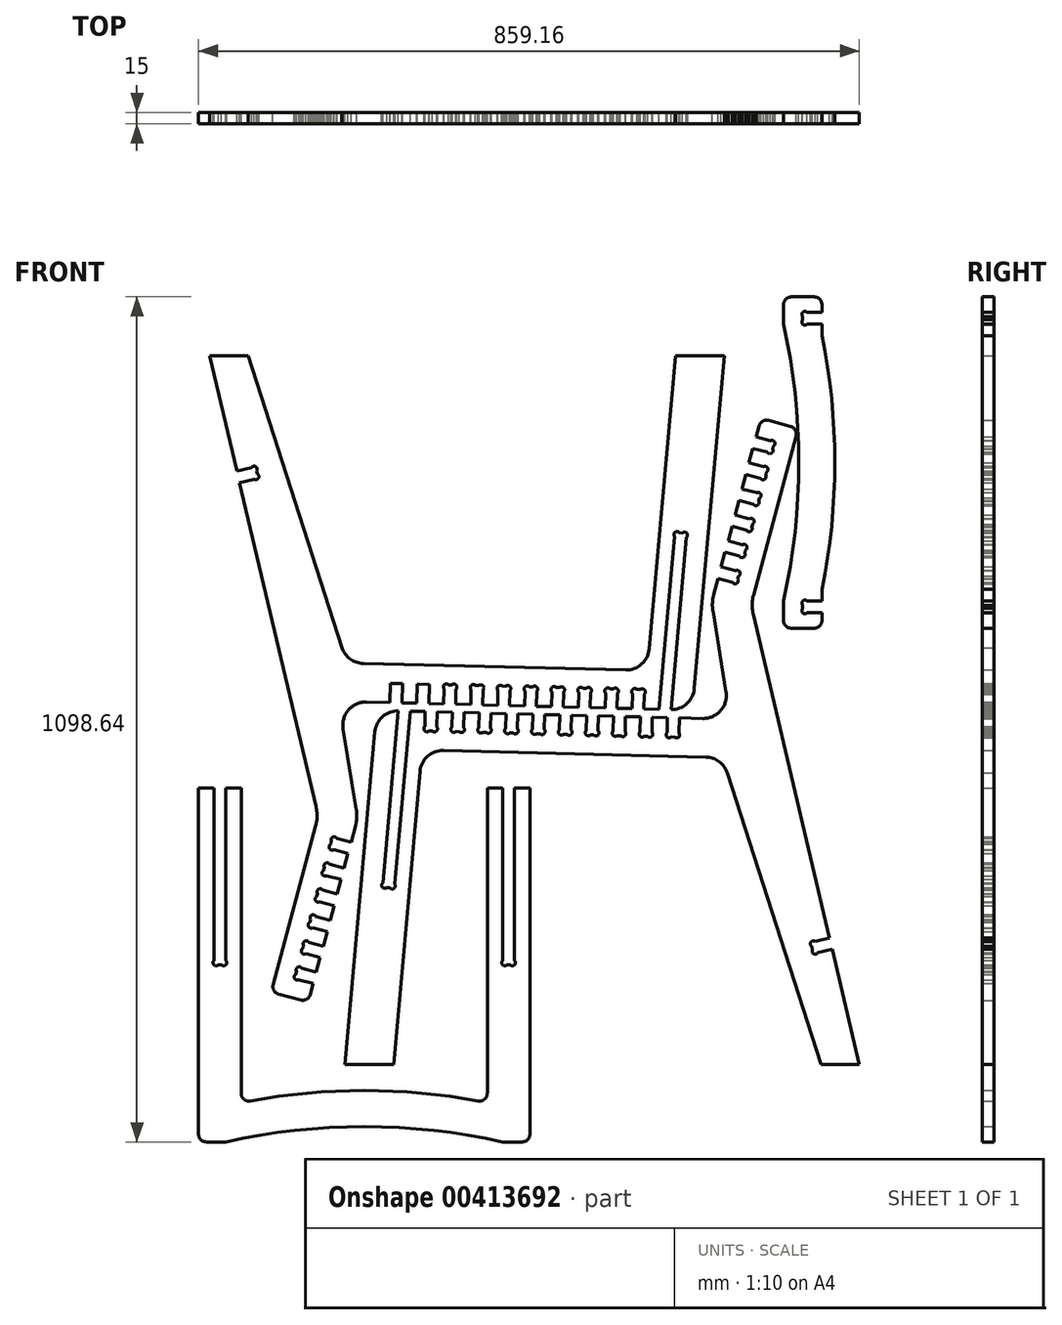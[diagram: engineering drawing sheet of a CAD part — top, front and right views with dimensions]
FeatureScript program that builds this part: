
annotation { "Feature Type Name" : "Feature", "Feature Type Description" : "" }
export const myFeature = defineFeature(function(context is Context, id is Id, definition is map)
    precondition{}
    {
        {
            var Q0;
            Q0=qCreatedBy(makeId("Front.planeOp"),FACE);
            var sketch = newSketch(context, id + "F0", { "sketchPlane" : qUnion([Q0])});
            skLineSegment(sketch, "E0", {"start": v(-375.2, 497.25) * mm, "end": v(-425.2, 497.25) * mm});
            skLineSegment(sketch, "E1", {"start": v(-425.2, 497.25) * mm, "end": v(-389.9, 347.46) * mm});
            skLineSegment(sketch, "E2", {"start": v(-389.9, 347.46) * mm, "end": v(-371.08, 351.9) * mm});
            skArc(sketch, "E3", {"start": v(-371.08, 351.9) * mm, "mid": v(-365.57, 353.2) * mm, "end": v(-364.28, 347.69) * mm});
            skLineSegment(sketch, "E4", {"start": v(-364.28, 347.69) * mm, "end": v(-363.34, 343.71) * mm});
            skArc(sketch, "E5", {"start": v(-363.34, 343.71) * mm, "mid": v(-362.04, 338.2) * mm, "end": v(-367.55, 336.91) * mm});
            skLineSegment(sketch, "E6", {"start": v(-367.55, 336.91) * mm, "end": v(-386.37, 332.48) * mm});
            skLineSegment(sketch, "E7", {"start": v(-386.37, 332.48) * mm, "end": v(-287.1, -88.96) * mm});
            skArc(sketch, "E8", {"start": v(-287.1, -88.96) * mm, "mid": v(-285.77, -101.18) * mm, "end": v(-287.47, -113.36) * mm});
            skLineSegment(sketch, "E9", {"start": v(-287.47, -113.36) * mm, "end": v(-342.89, -320.18) * mm});
            skArc(sketch, "E10", {"start": v(-342.89, -320.18) * mm, "mid": v(-341.89, -327.77) * mm, "end": v(-335.82, -332.42) * mm});
            skLineSegment(sketch, "E11", {"start": v(-335.82, -332.42) * mm, "end": v(-306.84, -340.19) * mm});
            skArc(sketch, "E12", {"start": v(-306.84, -340.19) * mm, "mid": v(-299.25, -339.19) * mm, "end": v(-294.6, -333.12) * mm});
            skLineSegment(sketch, "E13", {"start": v(-294.6, -333.12) * mm, "end": v(-290.77, -318.82) * mm});
            skLineSegment(sketch, "E14", {"start": v(-290.77, -318.82) * mm, "end": v(-309.45, -313.82) * mm});
            skArc(sketch, "E15", {"start": v(-309.45, -313.82) * mm, "mid": v(-314.91, -312.35) * mm, "end": v(-313.45, -306.9) * mm});
            skLineSegment(sketch, "E16", {"start": v(-313.45, -306.9) * mm, "end": v(-312.39, -302.94) * mm});
            skArc(sketch, "E17", {"start": v(-312.39, -302.94) * mm, "mid": v(-310.93, -297.48) * mm, "end": v(-305.46, -298.95) * mm});
            skLineSegment(sketch, "E18", {"start": v(-305.46, -298.95) * mm, "end": v(-286.78, -303.95) * mm});
            skLineSegment(sketch, "E19", {"start": v(-286.78, -303.95) * mm, "end": v(-281.7, -285.02) * mm});
            skLineSegment(sketch, "E20", {"start": v(-281.7, -285.02) * mm, "end": v(-300.39, -280.02) * mm});
            skArc(sketch, "E21", {"start": v(-300.39, -280.02) * mm, "mid": v(-305.85, -278.55) * mm, "end": v(-304.39, -273.09) * mm});
            skLineSegment(sketch, "E22", {"start": v(-304.39, -273.09) * mm, "end": v(-303.33, -269.14) * mm});
            skArc(sketch, "E23", {"start": v(-303.33, -269.14) * mm, "mid": v(-301.87, -263.68) * mm, "end": v(-296.4, -265.14) * mm});
            skLineSegment(sketch, "E24", {"start": v(-296.4, -265.14) * mm, "end": v(-277.72, -270.15) * mm});
            skLineSegment(sketch, "E25", {"start": v(-277.72, -270.15) * mm, "end": v(-272.65, -251.22) * mm});
            skLineSegment(sketch, "E26", {"start": v(-272.65, -251.22) * mm, "end": v(-291.33, -246.21) * mm});
            skArc(sketch, "E27", {"start": v(-291.33, -246.21) * mm, "mid": v(-296.8, -244.75) * mm, "end": v(-295.33, -239.29) * mm});
            skLineSegment(sketch, "E28", {"start": v(-295.33, -239.29) * mm, "end": v(-294.27, -235.34) * mm});
            skArc(sketch, "E29", {"start": v(-294.27, -235.34) * mm, "mid": v(-292.81, -229.88) * mm, "end": v(-287.35, -231.34) * mm});
            skLineSegment(sketch, "E30", {"start": v(-287.35, -231.34) * mm, "end": v(-268.66, -236.34) * mm});
            skLineSegment(sketch, "E31", {"start": v(-268.66, -236.34) * mm, "end": v(-263.6, -217.42) * mm});
            skLineSegment(sketch, "E32", {"start": v(-263.6, -217.42) * mm, "end": v(-282.27, -212.4) * mm});
            skArc(sketch, "E33", {"start": v(-282.27, -212.4) * mm, "mid": v(-287.74, -210.95) * mm, "end": v(-286.27, -205.48) * mm});
            skLineSegment(sketch, "E34", {"start": v(-286.27, -205.48) * mm, "end": v(-285.22, -201.54) * mm});
            skArc(sketch, "E35", {"start": v(-285.22, -201.54) * mm, "mid": v(-283.75, -196.07) * mm, "end": v(-278.29, -197.54) * mm});
            skLineSegment(sketch, "E36", {"start": v(-278.29, -197.54) * mm, "end": v(-259.6, -202.54) * mm});
            skLineSegment(sketch, "E37", {"start": v(-259.6, -202.54) * mm, "end": v(-254.54, -183.61) * mm});
            skLineSegment(sketch, "E38", {"start": v(-254.54, -183.61) * mm, "end": v(-273.22, -178.6) * mm});
            skArc(sketch, "E39", {"start": v(-273.22, -178.6) * mm, "mid": v(-278.68, -177.14) * mm, "end": v(-277.22, -171.68) * mm});
            skLineSegment(sketch, "E40", {"start": v(-277.22, -171.68) * mm, "end": v(-276.16, -167.73) * mm});
            skArc(sketch, "E41", {"start": v(-276.16, -167.73) * mm, "mid": v(-274.7, -162.27) * mm, "end": v(-269.23, -163.73) * mm});
            skLineSegment(sketch, "E42", {"start": v(-269.23, -163.73) * mm, "end": v(-250.55, -168.74) * mm});
            skLineSegment(sketch, "E43", {"start": v(-250.55, -168.74) * mm, "end": v(-245.48, -149.8) * mm});
            skLineSegment(sketch, "E44", {"start": v(-245.48, -149.8) * mm, "end": v(-264.16, -144.8) * mm});
            skArc(sketch, "E45", {"start": v(-264.16, -144.8) * mm, "mid": v(-269.62, -143.34) * mm, "end": v(-268.16, -137.88) * mm});
            skLineSegment(sketch, "E46", {"start": v(-268.16, -137.88) * mm, "end": v(-267.1, -133.93) * mm});
            skArc(sketch, "E47", {"start": v(-267.1, -133.93) * mm, "mid": v(-265.64, -128.47) * mm, "end": v(-260.17, -129.93) * mm});
            skLineSegment(sketch, "E48", {"start": v(-260.17, -129.93) * mm, "end": v(-241.5, -134.94) * mm});
            skLineSegment(sketch, "E49", {"start": v(-241.5, -134.94) * mm, "end": v(-235.8, -113.7) * mm});
            skArc(sketch, "E50", {"start": v(-235.8, -113.7) * mm, "mid": v(-234.15, -103.12) * mm, "end": v(-234.8, -92.43) * mm});
            skLineSegment(sketch, "E51", {"start": v(-234.8, -92.43) * mm, "end": v(-251.88, 12.44) * mm});
            skArc(sketch, "E52", {"start": v(-251.88, 12.44) * mm, "mid": v(-244.88, 36.98) * mm, "end": v(-221.53, 47.25) * mm});
            skLineSegment(sketch, "E53", {"start": v(-221.53, 47.25) * mm, "end": v(-190.95, 46.49) * mm});
            skLineSegment(sketch, "E54", {"start": v(-190.95, 46.49) * mm, "end": v(-190.33, 71.48) * mm});
            skLineSegment(sketch, "E55", {"start": v(-190.33, 71.48) * mm, "end": v(-174.93, 71.1) * mm});
            skLineSegment(sketch, "E56", {"start": v(-174.93, 71.1) * mm, "end": v(-175.56, 46.1) * mm});
            skLineSegment(sketch, "E57", {"start": v(-175.56, 46.1) * mm, "end": v(-155.97, 45.62) * mm});
            skLineSegment(sketch, "E58", {"start": v(-155.97, 45.62) * mm, "end": v(-155.34, 70.6) * mm});
            skLineSegment(sketch, "E59", {"start": v(-155.34, 70.6) * mm, "end": v(-139.95, 70.22) * mm});
            skLineSegment(sketch, "E60", {"start": v(-139.95, 70.22) * mm, "end": v(-140.57, 45.23) * mm});
            skLineSegment(sketch, "E61", {"start": v(-140.57, 45.23) * mm, "end": v(-120.98, 44.74) * mm});
            skLineSegment(sketch, "E62", {"start": v(-120.98, 44.74) * mm, "end": v(-120.5, 64.08) * mm});
            skArc(sketch, "E63", {"start": v(-120.5, 64.08) * mm, "mid": v(-120.36, 69.73) * mm, "end": v(-114.7, 69.6) * mm});
            skLineSegment(sketch, "E64", {"start": v(-114.7, 69.6) * mm, "end": v(-110.62, 69.5) * mm});
            skArc(sketch, "E65", {"start": v(-110.62, 69.5) * mm, "mid": v(-104.97, 69.35) * mm, "end": v(-105.1, 63.7) * mm});
            skLineSegment(sketch, "E66", {"start": v(-105.1, 63.7) * mm, "end": v(-105.59, 44.36) * mm});
            skLineSegment(sketch, "E67", {"start": v(-105.59, 44.36) * mm, "end": v(-86, 43.87) * mm});
            skLineSegment(sketch, "E68", {"start": v(-86, 43.87) * mm, "end": v(-85.51, 63.2) * mm});
            skArc(sketch, "E69", {"start": v(-85.51, 63.2) * mm, "mid": v(-85.37, 68.86) * mm, "end": v(-79.72, 68.72) * mm});
            skLineSegment(sketch, "E70", {"start": v(-79.72, 68.72) * mm, "end": v(-75.64, 68.62) * mm});
            skArc(sketch, "E71", {"start": v(-75.64, 68.62) * mm, "mid": v(-69.98, 68.48) * mm, "end": v(-70.12, 62.82) * mm});
            skLineSegment(sketch, "E72", {"start": v(-70.12, 62.82) * mm, "end": v(-70.6, 43.49) * mm});
            skLineSegment(sketch, "E73", {"start": v(-70.6, 43.49) * mm, "end": v(-51.01, 43) * mm});
            skLineSegment(sketch, "E74", {"start": v(-51.01, 43) * mm, "end": v(-50.53, 62.33) * mm});
            skArc(sketch, "E75", {"start": v(-50.53, 62.33) * mm, "mid": v(-50.39, 67.99) * mm, "end": v(-44.73, 67.85) * mm});
            skLineSegment(sketch, "E76", {"start": v(-44.73, 67.85) * mm, "end": v(-40.65, 67.75) * mm});
            skArc(sketch, "E77", {"start": v(-40.65, 67.75) * mm, "mid": v(-35, 67.6) * mm, "end": v(-35.14, 61.95) * mm});
            skLineSegment(sketch, "E78", {"start": v(-35.14, 61.95) * mm, "end": v(-35.62, 42.62) * mm});
            skLineSegment(sketch, "E79", {"start": v(-35.62, 42.62) * mm, "end": v(-16.03, 42.13) * mm});
            skLineSegment(sketch, "E80", {"start": v(-16.03, 42.13) * mm, "end": v(-15.55, 61.46) * mm});
            skArc(sketch, "E81", {"start": v(-15.55, 61.46) * mm, "mid": v(-15.4, 67.12) * mm, "end": v(-9.75, 66.98) * mm});
            skLineSegment(sketch, "E82", {"start": v(-9.75, 66.98) * mm, "end": v(-5.67, 66.87) * mm});
            skArc(sketch, "E83", {"start": v(-5.67, 66.87) * mm, "mid": v(-0.01, 66.73) * mm, "end": v(-0.15, 61.08) * mm});
            skLineSegment(sketch, "E84", {"start": v(-0.15, 61.08) * mm, "end": v(-0.63, 41.74) * mm});
            skLineSegment(sketch, "E85", {"start": v(-0.63, 41.74) * mm, "end": v(18.96, 41.26) * mm});
            skLineSegment(sketch, "E86", {"start": v(18.96, 41.26) * mm, "end": v(19.44, 60.6) * mm});
            skArc(sketch, "E87", {"start": v(19.44, 60.6) * mm, "mid": v(19.58, 66.24) * mm, "end": v(25.23, 66.1) * mm});
            skLineSegment(sketch, "E88", {"start": v(25.23, 66.1) * mm, "end": v(29.32, 66) * mm});
            skArc(sketch, "E89", {"start": v(29.32, 66) * mm, "mid": v(34.97, 65.86) * mm, "end": v(34.83, 60.2) * mm});
            skLineSegment(sketch, "E90", {"start": v(34.83, 60.2) * mm, "end": v(34.35, 40.87) * mm});
            skLineSegment(sketch, "E91", {"start": v(34.35, 40.87) * mm, "end": v(53.94, 40.38) * mm});
            skLineSegment(sketch, "E92", {"start": v(53.94, 40.38) * mm, "end": v(54.42, 59.72) * mm});
            skArc(sketch, "E93", {"start": v(54.42, 59.72) * mm, "mid": v(54.56, 65.37) * mm, "end": v(60.22, 65.23) * mm});
            skLineSegment(sketch, "E94", {"start": v(60.22, 65.23) * mm, "end": v(64.3, 65.13) * mm});
            skArc(sketch, "E95", {"start": v(64.3, 65.13) * mm, "mid": v(69.96, 64.99) * mm, "end": v(69.82, 59.33) * mm});
            skLineSegment(sketch, "E96", {"start": v(69.82, 59.33) * mm, "end": v(69.34, 40) * mm});
            skLineSegment(sketch, "E97", {"start": v(69.34, 40) * mm, "end": v(88.93, 39.51) * mm});
            skLineSegment(sketch, "E98", {"start": v(88.93, 39.51) * mm, "end": v(89.4, 58.85) * mm});
            skArc(sketch, "E99", {"start": v(89.4, 58.85) * mm, "mid": v(89.55, 64.5) * mm, "end": v(95.2, 64.36) * mm});
            skLineSegment(sketch, "E100", {"start": v(95.2, 64.36) * mm, "end": v(99.29, 64.26) * mm});
            skArc(sketch, "E101", {"start": v(99.29, 64.26) * mm, "mid": v(104.94, 64.12) * mm, "end": v(104.8, 58.46) * mm});
            skLineSegment(sketch, "E102", {"start": v(104.8, 58.46) * mm, "end": v(104.32, 39.13) * mm});
            skLineSegment(sketch, "E103", {"start": v(104.32, 39.13) * mm, "end": v(123.91, 38.64) * mm});
            skLineSegment(sketch, "E104", {"start": v(123.91, 38.64) * mm, "end": v(124.4, 57.97) * mm});
            skArc(sketch, "E105", {"start": v(124.4, 57.97) * mm, "mid": v(124.53, 63.63) * mm, "end": v(130.19, 63.49) * mm});
            skLineSegment(sketch, "E106", {"start": v(130.19, 63.49) * mm, "end": v(134.27, 63.39) * mm});
            skArc(sketch, "E107", {"start": v(134.27, 63.39) * mm, "mid": v(139.93, 63.24) * mm, "end": v(139.79, 57.6) * mm});
            skLineSegment(sketch, "E108", {"start": v(139.79, 57.6) * mm, "end": v(139.3, 38.26) * mm});
            skLineSegment(sketch, "E109", {"start": v(139.3, 38.26) * mm, "end": v(158.88, 37.77) * mm});
            skLineSegment(sketch, "E110", {"start": v(158.88, 37.77) * mm, "end": v(179.13, 262.38) * mm});
            skArc(sketch, "E111", {"start": v(179.13, 262.38) * mm, "mid": v(179.64, 268.01) * mm, "end": v(185.27, 267.5) * mm});
            skLineSegment(sketch, "E112", {"start": v(185.27, 267.5) * mm, "end": v(189.34, 267.14) * mm});
            skArc(sketch, "E113", {"start": v(189.34, 267.14) * mm, "mid": v(194.97, 266.63) * mm, "end": v(194.46, 261) * mm});
            skLineSegment(sketch, "E114", {"start": v(194.46, 261) * mm, "end": v(174.3, 37.38) * mm});
            skArc(sketch, "E115", {"start": v(174.3, 37.38) * mm, "mid": v(194.88, 45.05) * mm, "end": v(204.71, 64.68) * mm});
            skLineSegment(sketch, "E116", {"start": v(204.71, 64.68) * mm, "end": v(243.7, 497.25) * mm});
            skLineSegment(sketch, "E117", {"start": v(243.7, 497.25) * mm, "end": v(180.44, 497.25) * mm});
            skLineSegment(sketch, "E118", {"start": v(180.44, 497.25) * mm, "end": v(146.08, 116.15) * mm});
            skArc(sketch, "E119", {"start": v(146.08, 116.15) * mm, "mid": v(136.17, 96.45) * mm, "end": v(115.46, 88.86) * mm});
            skLineSegment(sketch, "E120", {"start": v(115.46, 88.86) * mm, "end": v(-225.61, 97.36) * mm});
            skArc(sketch, "E121", {"start": v(-225.61, 97.36) * mm, "mid": v(-242.67, 103.21) * mm, "end": v(-253.3, 117.79) * mm});
            skLineSegment(sketch, "E122", {"start": v(-253.3, 117.79) * mm, "end": v(-375.2, 497.25) * mm});
            skLineSegment(sketch, "E123", {"start": v(369.36, -424.14) * mm, "end": v(419.36, -424.14) * mm});
            skLineSegment(sketch, "E124", {"start": v(419.36, -424.14) * mm, "end": v(384.07, -274.36) * mm});
            skLineSegment(sketch, "E125", {"start": v(384.07, -274.36) * mm, "end": v(365.25, -278.8) * mm});
            skArc(sketch, "E126", {"start": v(365.25, -278.8) * mm, "mid": v(359.74, -280.09) * mm, "end": v(358.44, -274.58) * mm});
            skLineSegment(sketch, "E127", {"start": v(358.44, -274.58) * mm, "end": v(357.5, -270.6) * mm});
            skArc(sketch, "E128", {"start": v(357.5, -270.6) * mm, "mid": v(356.21, -265.1) * mm, "end": v(361.72, -263.8) * mm});
            skLineSegment(sketch, "E129", {"start": v(361.72, -263.8) * mm, "end": v(380.54, -259.37) * mm});
            skLineSegment(sketch, "E130", {"start": v(380.54, -259.37) * mm, "end": v(281.26, 162.06) * mm});
            skArc(sketch, "E131", {"start": v(281.26, 162.06) * mm, "mid": v(279.94, 174.29) * mm, "end": v(281.64, 186.46) * mm});
            skLineSegment(sketch, "E132", {"start": v(281.64, 186.46) * mm, "end": v(337.05, 393.28) * mm});
            skArc(sketch, "E133", {"start": v(337.05, 393.28) * mm, "mid": v(336.05, 400.87) * mm, "end": v(329.98, 405.53) * mm});
            skLineSegment(sketch, "E134", {"start": v(329.98, 405.53) * mm, "end": v(301, 413.3) * mm});
            skArc(sketch, "E135", {"start": v(301, 413.3) * mm, "mid": v(293.42, 412.3) * mm, "end": v(288.76, 406.22) * mm});
            skLineSegment(sketch, "E136", {"start": v(288.76, 406.22) * mm, "end": v(284.93, 391.93) * mm});
            skLineSegment(sketch, "E137", {"start": v(284.93, 391.93) * mm, "end": v(303.61, 386.92) * mm});
            skArc(sketch, "E138", {"start": v(303.61, 386.92) * mm, "mid": v(309.08, 385.46) * mm, "end": v(307.61, 380) * mm});
            skLineSegment(sketch, "E139", {"start": v(307.61, 380) * mm, "end": v(306.56, 376.05) * mm});
            skArc(sketch, "E140", {"start": v(306.56, 376.05) * mm, "mid": v(305.1, 370.59) * mm, "end": v(299.63, 372.05) * mm});
            skLineSegment(sketch, "E141", {"start": v(299.63, 372.05) * mm, "end": v(280.95, 377.06) * mm});
            skLineSegment(sketch, "E142", {"start": v(280.95, 377.06) * mm, "end": v(275.87, 358.13) * mm});
            skLineSegment(sketch, "E143", {"start": v(275.87, 358.13) * mm, "end": v(294.56, 353.12) * mm});
            skArc(sketch, "E144", {"start": v(294.56, 353.12) * mm, "mid": v(300.02, 351.66) * mm, "end": v(298.56, 346.2) * mm});
            skLineSegment(sketch, "E145", {"start": v(298.56, 346.2) * mm, "end": v(297.5, 342.25) * mm});
            skArc(sketch, "E146", {"start": v(297.5, 342.25) * mm, "mid": v(296.03, 336.78) * mm, "end": v(290.57, 338.25) * mm});
            skLineSegment(sketch, "E147", {"start": v(290.57, 338.25) * mm, "end": v(271.89, 343.25) * mm});
            skLineSegment(sketch, "E148", {"start": v(271.89, 343.25) * mm, "end": v(266.82, 324.32) * mm});
            skLineSegment(sketch, "E149", {"start": v(266.82, 324.32) * mm, "end": v(285.5, 319.32) * mm});
            skArc(sketch, "E150", {"start": v(285.5, 319.32) * mm, "mid": v(290.96, 317.85) * mm, "end": v(289.5, 312.4) * mm});
            skLineSegment(sketch, "E151", {"start": v(289.5, 312.4) * mm, "end": v(288.44, 308.44) * mm});
            skArc(sketch, "E152", {"start": v(288.44, 308.44) * mm, "mid": v(286.98, 302.98) * mm, "end": v(281.51, 304.44) * mm});
            skLineSegment(sketch, "E153", {"start": v(281.51, 304.44) * mm, "end": v(262.83, 309.45) * mm});
            skLineSegment(sketch, "E154", {"start": v(262.83, 309.45) * mm, "end": v(257.76, 290.52) * mm});
            skLineSegment(sketch, "E155", {"start": v(257.76, 290.52) * mm, "end": v(276.44, 285.51) * mm});
            skArc(sketch, "E156", {"start": v(276.44, 285.51) * mm, "mid": v(281.9, 284.05) * mm, "end": v(280.44, 278.59) * mm});
            skLineSegment(sketch, "E157", {"start": v(280.44, 278.59) * mm, "end": v(279.38, 274.64) * mm});
            skArc(sketch, "E158", {"start": v(279.38, 274.64) * mm, "mid": v(277.92, 269.18) * mm, "end": v(272.46, 270.64) * mm});
            skLineSegment(sketch, "E159", {"start": v(272.46, 270.64) * mm, "end": v(253.77, 275.65) * mm});
            skLineSegment(sketch, "E160", {"start": v(253.77, 275.65) * mm, "end": v(248.7, 256.72) * mm});
            skLineSegment(sketch, "E161", {"start": v(248.7, 256.72) * mm, "end": v(267.38, 251.71) * mm});
            skArc(sketch, "E162", {"start": v(267.38, 251.71) * mm, "mid": v(272.85, 250.25) * mm, "end": v(271.38, 244.78) * mm});
            skLineSegment(sketch, "E163", {"start": v(271.38, 244.78) * mm, "end": v(270.33, 240.84) * mm});
            skArc(sketch, "E164", {"start": v(270.33, 240.84) * mm, "mid": v(268.86, 235.37) * mm, "end": v(263.4, 236.84) * mm});
            skLineSegment(sketch, "E165", {"start": v(263.4, 236.84) * mm, "end": v(244.72, 241.84) * mm});
            skLineSegment(sketch, "E166", {"start": v(244.72, 241.84) * mm, "end": v(239.64, 222.91) * mm});
            skLineSegment(sketch, "E167", {"start": v(239.64, 222.91) * mm, "end": v(258.33, 217.9) * mm});
            skArc(sketch, "E168", {"start": v(258.33, 217.9) * mm, "mid": v(263.79, 216.44) * mm, "end": v(262.33, 210.98) * mm});
            skLineSegment(sketch, "E169", {"start": v(262.33, 210.98) * mm, "end": v(261.27, 207.03) * mm});
            skArc(sketch, "E170", {"start": v(261.27, 207.03) * mm, "mid": v(259.8, 201.57) * mm, "end": v(254.34, 203.03) * mm});
            skLineSegment(sketch, "E171", {"start": v(254.34, 203.03) * mm, "end": v(235.66, 208.04) * mm});
            skLineSegment(sketch, "E172", {"start": v(235.66, 208.04) * mm, "end": v(229.97, 186.8) * mm});
            skArc(sketch, "E173", {"start": v(229.97, 186.8) * mm, "mid": v(228.32, 176.22) * mm, "end": v(228.96, 165.54) * mm});
            skLineSegment(sketch, "E174", {"start": v(228.96, 165.54) * mm, "end": v(246.05, 60.66) * mm});
            skArc(sketch, "E175", {"start": v(246.05, 60.66) * mm, "mid": v(239.05, 36.13) * mm, "end": v(215.7, 25.86) * mm});
            skLineSegment(sketch, "E176", {"start": v(215.7, 25.86) * mm, "end": v(185.12, 26.62) * mm});
            skLineSegment(sketch, "E177", {"start": v(185.12, 26.62) * mm, "end": v(184.64, 7.28) * mm});
            skArc(sketch, "E178", {"start": v(184.64, 7.28) * mm, "mid": v(184.5, 1.63) * mm, "end": v(178.84, 1.77) * mm});
            skLineSegment(sketch, "E179", {"start": v(178.84, 1.77) * mm, "end": v(174.76, 1.87) * mm});
            skArc(sketch, "E180", {"start": v(174.76, 1.87) * mm, "mid": v(169.1, 2.01) * mm, "end": v(169.24, 7.67) * mm});
            skLineSegment(sketch, "E181", {"start": v(169.24, 7.67) * mm, "end": v(169.72, 27) * mm});
            skLineSegment(sketch, "E182", {"start": v(169.72, 27) * mm, "end": v(150.13, 27.49) * mm});
            skLineSegment(sketch, "E183", {"start": v(150.13, 27.49) * mm, "end": v(149.65, 8.15) * mm});
            skArc(sketch, "E184", {"start": v(149.65, 8.15) * mm, "mid": v(149.51, 2.5) * mm, "end": v(143.86, 2.64) * mm});
            skLineSegment(sketch, "E185", {"start": v(143.86, 2.64) * mm, "end": v(139.77, 2.74) * mm});
            skArc(sketch, "E186", {"start": v(139.77, 2.74) * mm, "mid": v(134.12, 2.88) * mm, "end": v(134.26, 8.54) * mm});
            skLineSegment(sketch, "E187", {"start": v(134.26, 8.54) * mm, "end": v(134.74, 27.87) * mm});
            skLineSegment(sketch, "E188", {"start": v(134.74, 27.87) * mm, "end": v(115.15, 28.36) * mm});
            skLineSegment(sketch, "E189", {"start": v(115.15, 28.36) * mm, "end": v(114.67, 9.03) * mm});
            skArc(sketch, "E190", {"start": v(114.67, 9.03) * mm, "mid": v(114.53, 3.37) * mm, "end": v(108.87, 3.51) * mm});
            skLineSegment(sketch, "E191", {"start": v(108.87, 3.51) * mm, "end": v(104.79, 3.62) * mm});
            skArc(sketch, "E192", {"start": v(104.79, 3.62) * mm, "mid": v(99.13, 3.76) * mm, "end": v(99.27, 9.41) * mm});
            skLineSegment(sketch, "E193", {"start": v(99.27, 9.41) * mm, "end": v(99.76, 28.75) * mm});
            skLineSegment(sketch, "E194", {"start": v(99.76, 28.75) * mm, "end": v(80.16, 29.23) * mm});
            skLineSegment(sketch, "E195", {"start": v(80.16, 29.23) * mm, "end": v(79.68, 9.9) * mm});
            skArc(sketch, "E196", {"start": v(79.68, 9.9) * mm, "mid": v(79.54, 4.24) * mm, "end": v(73.89, 4.39) * mm});
            skLineSegment(sketch, "E197", {"start": v(73.89, 4.39) * mm, "end": v(69.8, 4.49) * mm});
            skArc(sketch, "E198", {"start": v(69.8, 4.49) * mm, "mid": v(64.15, 4.63) * mm, "end": v(64.29, 10.28) * mm});
            skLineSegment(sketch, "E199", {"start": v(64.29, 10.28) * mm, "end": v(64.77, 29.62) * mm});
            skLineSegment(sketch, "E200", {"start": v(64.77, 29.62) * mm, "end": v(45.18, 30.1) * mm});
            skLineSegment(sketch, "E201", {"start": v(45.18, 30.1) * mm, "end": v(44.7, 10.77) * mm});
            skArc(sketch, "E202", {"start": v(44.7, 10.77) * mm, "mid": v(44.56, 5.12) * mm, "end": v(38.9, 5.26) * mm});
            skLineSegment(sketch, "E203", {"start": v(38.9, 5.26) * mm, "end": v(34.82, 5.36) * mm});
            skArc(sketch, "E204", {"start": v(34.82, 5.36) * mm, "mid": v(29.16, 5.5) * mm, "end": v(29.3, 11.15) * mm});
            skLineSegment(sketch, "E205", {"start": v(29.3, 11.15) * mm, "end": v(29.79, 30.49) * mm});
            skLineSegment(sketch, "E206", {"start": v(29.79, 30.49) * mm, "end": v(10.2, 30.98) * mm});
            skLineSegment(sketch, "E207", {"start": v(10.2, 30.98) * mm, "end": v(9.71, 11.64) * mm});
            skArc(sketch, "E208", {"start": v(9.71, 11.64) * mm, "mid": v(9.57, 5.99) * mm, "end": v(3.92, 6.13) * mm});
            skLineSegment(sketch, "E209", {"start": v(3.92, 6.13) * mm, "end": v(-0.17, 6.23) * mm});
            skArc(sketch, "E210", {"start": v(-0.17, 6.23) * mm, "mid": v(-5.82, 6.37) * mm, "end": v(-5.68, 12.03) * mm});
            skLineSegment(sketch, "E211", {"start": v(-5.68, 12.03) * mm, "end": v(-5.2, 31.36) * mm});
            skLineSegment(sketch, "E212", {"start": v(-5.2, 31.36) * mm, "end": v(-24.8, 31.85) * mm});
            skLineSegment(sketch, "E213", {"start": v(-24.8, 31.85) * mm, "end": v(-25.27, 12.52) * mm});
            skArc(sketch, "E214", {"start": v(-25.27, 12.52) * mm, "mid": v(-25.41, 6.86) * mm, "end": v(-31.07, 7) * mm});
            skLineSegment(sketch, "E215", {"start": v(-31.07, 7) * mm, "end": v(-35.15, 7.1) * mm});
            skArc(sketch, "E216", {"start": v(-35.15, 7.1) * mm, "mid": v(-40.8, 7.24) * mm, "end": v(-40.67, 12.9) * mm});
            skLineSegment(sketch, "E217", {"start": v(-40.67, 12.9) * mm, "end": v(-40.18, 32.23) * mm});
            skLineSegment(sketch, "E218", {"start": v(-40.18, 32.23) * mm, "end": v(-59.78, 32.72) * mm});
            skLineSegment(sketch, "E219", {"start": v(-59.78, 32.72) * mm, "end": v(-60.26, 13.39) * mm});
            skArc(sketch, "E220", {"start": v(-60.26, 13.39) * mm, "mid": v(-60.4, 7.73) * mm, "end": v(-66.05, 7.87) * mm});
            skLineSegment(sketch, "E221", {"start": v(-66.05, 7.87) * mm, "end": v(-70.14, 7.98) * mm});
            skArc(sketch, "E222", {"start": v(-70.14, 7.98) * mm, "mid": v(-75.8, 8.12) * mm, "end": v(-75.65, 13.77) * mm});
            skLineSegment(sketch, "E223", {"start": v(-75.65, 13.77) * mm, "end": v(-75.17, 33.1) * mm});
            skLineSegment(sketch, "E224", {"start": v(-75.17, 33.1) * mm, "end": v(-94.76, 33.6) * mm});
            skLineSegment(sketch, "E225", {"start": v(-94.76, 33.6) * mm, "end": v(-95.24, 14.26) * mm});
            skArc(sketch, "E226", {"start": v(-95.24, 14.26) * mm, "mid": v(-95.38, 8.6) * mm, "end": v(-101.04, 8.75) * mm});
            skLineSegment(sketch, "E227", {"start": v(-101.04, 8.75) * mm, "end": v(-105.12, 8.85) * mm});
            skArc(sketch, "E228", {"start": v(-105.12, 8.85) * mm, "mid": v(-110.78, 8.99) * mm, "end": v(-110.64, 14.64) * mm});
            skLineSegment(sketch, "E229", {"start": v(-110.64, 14.64) * mm, "end": v(-110.15, 33.98) * mm});
            skLineSegment(sketch, "E230", {"start": v(-110.15, 33.98) * mm, "end": v(-129.74, 34.47) * mm});
            skLineSegment(sketch, "E231", {"start": v(-129.74, 34.47) * mm, "end": v(-130.23, 15.13) * mm});
            skArc(sketch, "E232", {"start": v(-130.23, 15.13) * mm, "mid": v(-130.37, 9.48) * mm, "end": v(-136.02, 9.62) * mm});
            skLineSegment(sketch, "E233", {"start": v(-136.02, 9.62) * mm, "end": v(-140.1, 9.72) * mm});
            skArc(sketch, "E234", {"start": v(-140.1, 9.72) * mm, "mid": v(-145.76, 9.86) * mm, "end": v(-145.62, 15.52) * mm});
            skLineSegment(sketch, "E235", {"start": v(-145.62, 15.52) * mm, "end": v(-145.14, 34.85) * mm});
            skLineSegment(sketch, "E236", {"start": v(-145.14, 34.85) * mm, "end": v(-164.71, 35.34) * mm});
            skLineSegment(sketch, "E237", {"start": v(-164.71, 35.34) * mm, "end": v(-184.96, -189.27) * mm});
            skArc(sketch, "E238", {"start": v(-184.96, -189.27) * mm, "mid": v(-185.47, -194.9) * mm, "end": v(-191.1, -194.4) * mm});
            skLineSegment(sketch, "E239", {"start": v(-191.1, -194.4) * mm, "end": v(-195.17, -194.03) * mm});
            skArc(sketch, "E240", {"start": v(-195.17, -194.03) * mm, "mid": v(-200.8, -193.52) * mm, "end": v(-200.3, -187.89) * mm});
            skLineSegment(sketch, "E241", {"start": v(-200.3, -187.89) * mm, "end": v(-180.14, 35.72) * mm});
            skArc(sketch, "E242", {"start": v(-180.14, 35.72) * mm, "mid": v(-200.7, 28.05) * mm, "end": v(-210.55, 8.42) * mm});
            skLineSegment(sketch, "E243", {"start": v(-210.55, 8.42) * mm, "end": v(-249.54, -424.14) * mm});
            skLineSegment(sketch, "E244", {"start": v(-249.54, -424.14) * mm, "end": v(-186.27, -424.14) * mm});
            skLineSegment(sketch, "E245", {"start": v(-186.27, -424.14) * mm, "end": v(-151.92, -43.05) * mm});
            skArc(sketch, "E246", {"start": v(-151.92, -43.05) * mm, "mid": v(-142, -23.35) * mm, "end": v(-121.3, -15.75) * mm});
            skLineSegment(sketch, "E247", {"start": v(-121.3, -15.75) * mm, "end": v(219.78, -24.26) * mm});
            skArc(sketch, "E248", {"start": v(219.78, -24.26) * mm, "mid": v(236.84, -30.1) * mm, "end": v(247.46, -44.68) * mm});
            skLineSegment(sketch, "E249", {"start": v(247.46, -44.68) * mm, "end": v(369.36, -424.14) * mm});
            skLineSegment(sketch, "E250", {"start": v(-9.05, -64.32) * mm, "end": v(-29.05, -64.32) * mm});
            skLineSegment(sketch, "E251", {"start": v(-29.05, -64.32) * mm, "end": v(-29.05, -288.85) * mm});
            skArc(sketch, "E252", {"start": v(-29.05, -288.85) * mm, "mid": v(-29.05, -294.5) * mm, "end": v(-34.7, -294.5) * mm});
            skLineSegment(sketch, "E253", {"start": v(-34.7, -294.5) * mm, "end": v(-38.8, -294.5) * mm});
            skArc(sketch, "E254", {"start": v(-38.8, -294.5) * mm, "mid": v(-44.45, -294.5) * mm, "end": v(-44.45, -288.85) * mm});
            skLineSegment(sketch, "E255", {"start": v(-44.45, -288.85) * mm, "end": v(-44.45, -64.32) * mm});
            skLineSegment(sketch, "E256", {"start": v(-44.45, -64.32) * mm, "end": v(-64.45, -64.32) * mm});
            skLineSegment(sketch, "E257", {"start": v(-64.45, -64.32) * mm, "end": v(-64.45, -461.6) * mm});
            skArc(sketch, "E258", {"start": v(-64.45, -461.6) * mm, "mid": v(-68.05, -469.29) * mm, "end": v(-76.25, -471.44) * mm});
            skArc(sketch, "E259", {"start": v(-76.25, -471.44) * mm, "mid": v(-224.43, -457.94) * mm, "end": v(-372.6, -471.44) * mm});
            skArc(sketch, "E260", {"start": v(-372.6, -471.44) * mm, "mid": v(-380.8, -469.29) * mm, "end": v(-384.4, -461.6) * mm});
            skLineSegment(sketch, "E261", {"start": v(-384.4, -461.6) * mm, "end": v(-384.4, -64.32) * mm});
            skLineSegment(sketch, "E262", {"start": v(-384.4, -64.32) * mm, "end": v(-404.4, -64.32) * mm});
            skLineSegment(sketch, "E263", {"start": v(-404.4, -64.32) * mm, "end": v(-404.4, -288.85) * mm});
            skArc(sketch, "E264", {"start": v(-404.4, -288.85) * mm, "mid": v(-404.4, -294.5) * mm, "end": v(-410.06, -294.5) * mm});
            skLineSegment(sketch, "E265", {"start": v(-410.06, -294.5) * mm, "end": v(-414.14, -294.5) * mm});
            skArc(sketch, "E266", {"start": v(-414.14, -294.5) * mm, "mid": v(-419.8, -294.5) * mm, "end": v(-419.8, -288.85) * mm});
            skLineSegment(sketch, "E267", {"start": v(-419.8, -288.85) * mm, "end": v(-419.8, -64.32) * mm});
            skLineSegment(sketch, "E268", {"start": v(-419.8, -64.32) * mm, "end": v(-439.8, -64.32) * mm});
            skLineSegment(sketch, "E269", {"start": v(-439.8, -64.32) * mm, "end": v(-439.8, -514.7) * mm});
            skArc(sketch, "E270", {"start": v(-439.8, -514.7) * mm, "mid": v(-436.87, -521.77) * mm, "end": v(-429.8, -524.7) * mm});
            skLineSegment(sketch, "E271", {"start": v(-429.8, -524.7) * mm, "end": v(-404.37, -524.7) * mm});
            skArc(sketch, "E272", {"start": v(-404.37, -524.7) * mm, "mid": v(-224.43, -504.7) * mm, "end": v(-44.48, -524.7) * mm});
            skLineSegment(sketch, "E273", {"start": v(-44.48, -524.7) * mm, "end": v(-19.05, -524.7) * mm});
            skArc(sketch, "E274", {"start": v(-19.05, -524.7) * mm, "mid": v(-11.98, -521.77) * mm, "end": v(-9.05, -514.7) * mm});
            skLineSegment(sketch, "E275", {"start": v(-9.05, -514.7) * mm, "end": v(-9.05, -64.32) * mm});
            skLineSegment(sketch, "E276", {"start": v(320.68, 178.62) * mm, "end": v(320.68, 153.19) * mm});
            skArc(sketch, "E277", {"start": v(320.68, 153.19) * mm, "mid": v(323.6, 146.12) * mm, "end": v(330.67, 143.2) * mm});
            skLineSegment(sketch, "E278", {"start": v(330.67, 143.2) * mm, "end": v(360.66, 143.2) * mm});
            skArc(sketch, "E279", {"start": v(360.66, 143.2) * mm, "mid": v(367.73, 146.12) * mm, "end": v(370.66, 153.19) * mm});
            skLineSegment(sketch, "E280", {"start": v(370.66, 153.19) * mm, "end": v(370.66, 163.19) * mm});
            skLineSegment(sketch, "E281", {"start": v(370.66, 163.19) * mm, "end": v(351.32, 163.19) * mm});
            skArc(sketch, "E282", {"start": v(351.32, 163.19) * mm, "mid": v(345.67, 163.19) * mm, "end": v(345.67, 168.84) * mm});
            skLineSegment(sketch, "E283", {"start": v(345.67, 168.84) * mm, "end": v(345.67, 172.93) * mm});
            skArc(sketch, "E284", {"start": v(345.67, 172.93) * mm, "mid": v(345.67, 178.59) * mm, "end": v(351.32, 178.59) * mm});
            skLineSegment(sketch, "E285", {"start": v(351.32, 178.59) * mm, "end": v(370.66, 178.59) * mm});
            skLineSegment(sketch, "E286", {"start": v(370.66, 178.59) * mm, "end": v(370.66, 193.58) * mm});
            skArc(sketch, "E287", {"start": v(370.66, 193.58) * mm, "mid": v(387.44, 358.56) * mm, "end": v(370.66, 523.54) * mm});
            skLineSegment(sketch, "E288", {"start": v(370.66, 523.54) * mm, "end": v(370.66, 538.54) * mm});
            skLineSegment(sketch, "E289", {"start": v(370.66, 538.54) * mm, "end": v(351.32, 538.54) * mm});
            skArc(sketch, "E290", {"start": v(351.32, 538.54) * mm, "mid": v(345.67, 538.54) * mm, "end": v(345.67, 544.2) * mm});
            skLineSegment(sketch, "E291", {"start": v(345.67, 544.2) * mm, "end": v(345.67, 548.28) * mm});
            skArc(sketch, "E292", {"start": v(345.67, 548.28) * mm, "mid": v(345.67, 553.94) * mm, "end": v(351.32, 553.94) * mm});
            skLineSegment(sketch, "E293", {"start": v(351.32, 553.94) * mm, "end": v(370.66, 553.94) * mm});
            skLineSegment(sketch, "E294", {"start": v(370.66, 553.94) * mm, "end": v(370.66, 563.94) * mm});
            skArc(sketch, "E295", {"start": v(370.66, 563.94) * mm, "mid": v(367.73, 571) * mm, "end": v(360.66, 573.94) * mm});
            skLineSegment(sketch, "E296", {"start": v(360.66, 573.94) * mm, "end": v(330.67, 573.94) * mm});
            skArc(sketch, "E297", {"start": v(330.67, 573.94) * mm, "mid": v(323.6, 571) * mm, "end": v(320.68, 563.94) * mm});
            skLineSegment(sketch, "E298", {"start": v(320.68, 563.94) * mm, "end": v(320.68, 538.5) * mm});
            skArc(sketch, "E299", {"start": v(320.68, 538.5) * mm, "mid": v(340.67, 358.56) * mm, "end": v(320.68, 178.62) * mm});
            skSolve(sketch);
        }
        {
            var Q0;
            Q0 = qSketchRegion(id + "F0", true);
            extrude(context, id + "F1", {"entities" : qUnion([Q0]), "depth" : 15 * mm});
        }
    });
